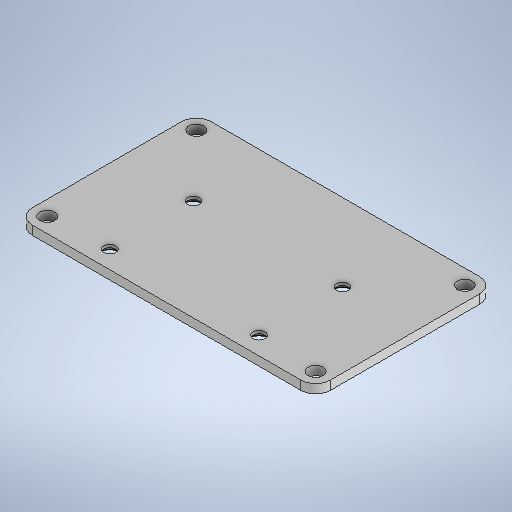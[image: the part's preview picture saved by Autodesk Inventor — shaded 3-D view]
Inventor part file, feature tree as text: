
AUTODESK INVENTOR PART (.ipt)
format: ipt  version: 2025.1 (Build 291241000, 241)  size: 269,824 bytes
history: native  units: mm
features: sketch x3, hole x2, sheet_metal_op x1, fillet x1, other x1
ambient origin geometry x8: Origin, YZ Plane, XZ Plane, XY Plane, X Axis, Y Axis, Z Axis, Center Point
bodies: Solid1 (feature_tree)
feature tree (8):
  sheet_metal_op  "Face1"
  hole  "Hole1"  [1 undecoded]
  hole  "Hole2"  [1 undecoded]
  fillet  "Fillet1"  Radius=5.0mm
  sketch  "Sketch1"  dims[d0=60.0mm d1=100.0mm]
  other  "Plate1"
  sketch  "Sketch2"  dims[d2=3.0mm d3=5.0mm d4=5.0mm]
  sketch  "Sketch3"  dims[d5=5.0mm d6=5.0mm d7=5.0mm d8=5.0mm d9=6.0mm d10=4.0mm d11=2.0mm d12=90.0deg d13=3.0mm d14=20.594885mm d15=28.0mm d16=6.0mm d17=50.0mm d18=25.0mm d19=4.0mm d20=6.0mm d21=8.0mm d22=2.0mm d23=90.0deg d24=8.0mm d25=20.594885mm d26=5.0mm]
note: 2 required parameter values undecoded (feature->parameter linkage not recoverable at this tier; creation-order binding heuristic only, values carry confidence <= 0.55)
